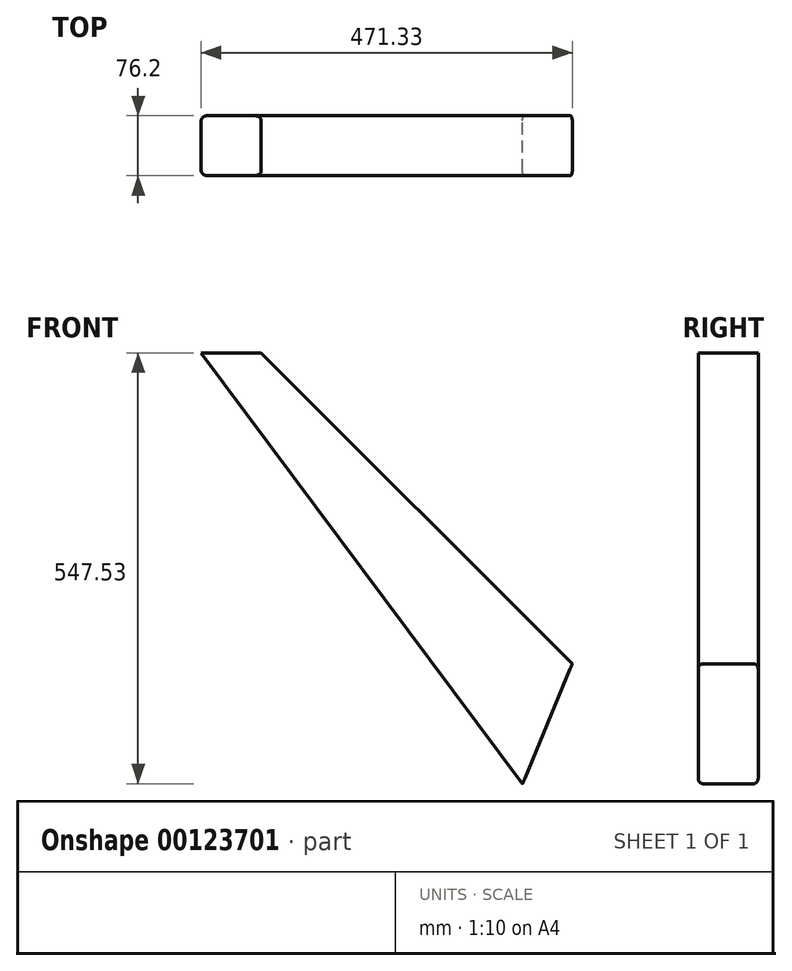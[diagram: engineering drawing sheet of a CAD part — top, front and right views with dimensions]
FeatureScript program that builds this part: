
annotation { "Feature Type Name" : "Feature", "Feature Type Description" : "" }
export const myFeature = defineFeature(function(context is Context, id is Id, definition is map)
    precondition{}
    {
        {
            var Q0;
            Q0=qCreatedBy(makeId("Front.planeOp"),FACE);
            var sketch = newSketch(context, id + "F0", { "sketchPlane" : qUnion([Q0])});
            skLineSegment(sketch, "E0", {"start": v(-218.92, 284.73) * mm, "end": v(176.21, -110.4) * mm});
            skLineSegment(sketch, "E1", {"start": v(176.21, -110.4) * mm, "end": v(113.08, -262.8) * mm});
            skLineSegment(sketch, "E2", {"start": v(113.08, -262.8) * mm, "end": v(-295.12, 284.73) * mm});
            skLineSegment(sketch, "E3", {"start": v(-295.12, 284.73) * mm, "end": v(-218.92, 284.73) * mm});
            skSolve(sketch);
        }
        {
            var Q0;
            Q0=makeQuery(id+"F0.imprint","IMPRINT",FACE,{"disambiguationData":[TD([[makeQuery(id+"F0.imprint","IMPRINT",EDGE,{"derivedFrom":sQuery(id+"F0.wireOp",EDGE,"E0")}),-1.0]])]});
            extrude(context, id + "F1", {"entities" : qUnion([Q0]), "depth" : 76.2 * mm});
        }
        {
            var Q0;
            Q0=makeQuery(id+"F1.opExtrude","CAP_EDGE",EDGE,{"disambiguationData":[OSD([sQuery(id+"F0.wireOp",EDGE,"E0")])],"isStart":false});
            var Q1;
            Q1=makeQuery(id+"F1.opExtrude","CAP_EDGE",EDGE,{"disambiguationData":[OSD([sQuery(id+"F0.wireOp",EDGE,"E0")])],"isStart":true});
            var Q2;
            Q2=makeQuery(id+"F1.opExtrude","CAP_EDGE",EDGE,{"disambiguationData":[OSD([sQuery(id+"F0.wireOp",EDGE,"E2")])],"isStart":false});
            var Q3;
            Q3=makeQuery(id+"F1.opExtrude","CAP_EDGE",EDGE,{"disambiguationData":[OSD([sQuery(id+"F0.wireOp",EDGE,"E2")])],"isStart":true});
            fillet(context, id + "F2", {"entities" : qUnion([Q0, Q1, Q2, Q3]), "radius" : 6.35 * mm, "tangentPropagation" : true, "allowEdgeOverflow" : false});
        }
    });
